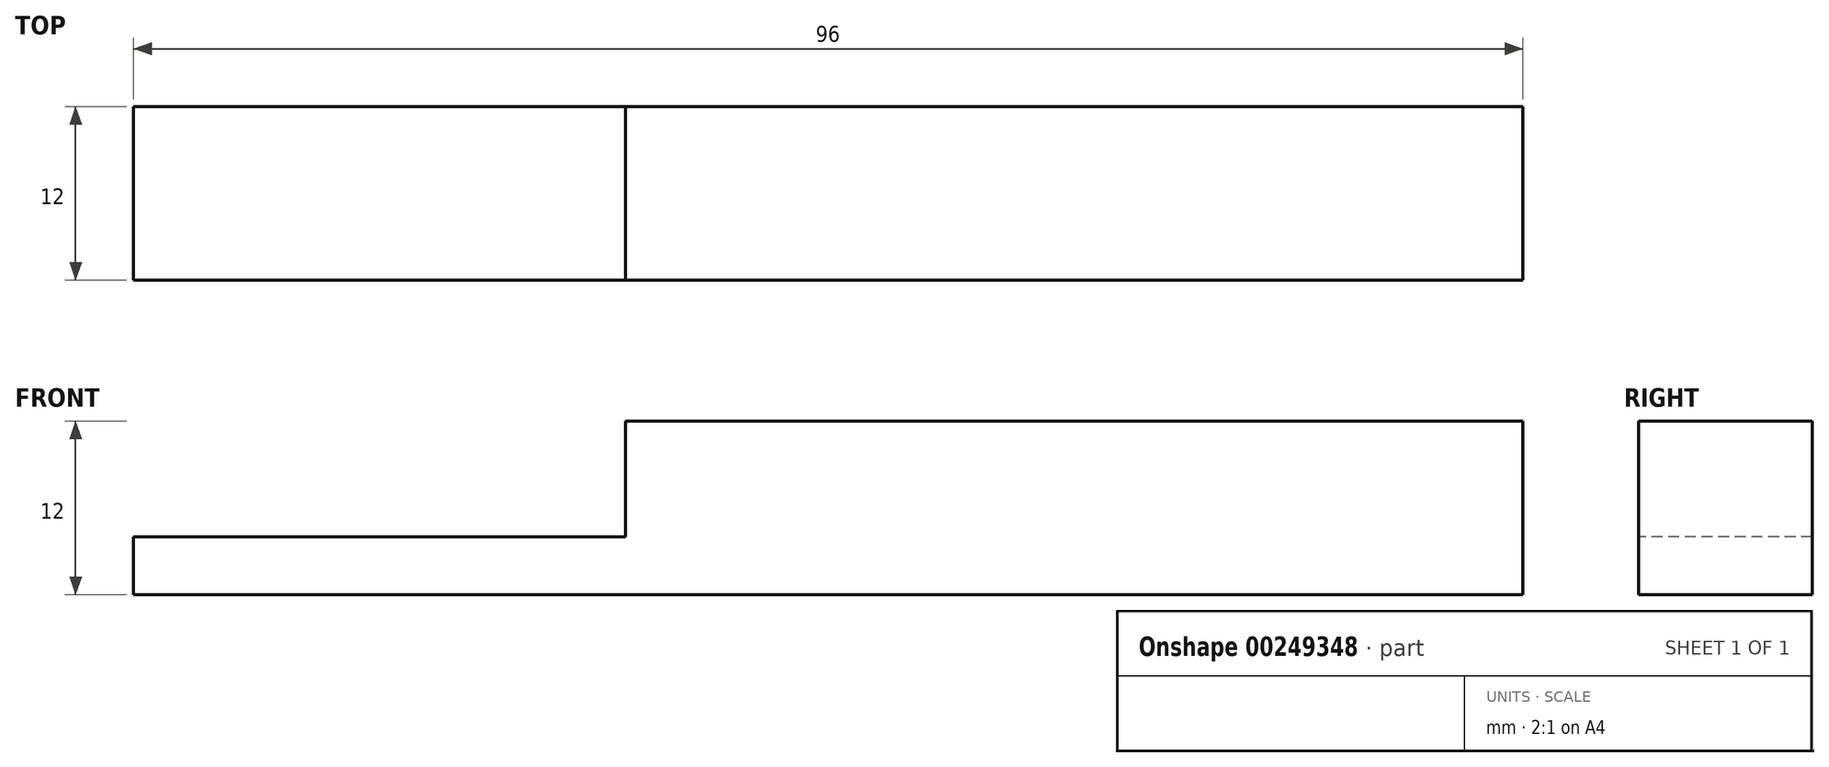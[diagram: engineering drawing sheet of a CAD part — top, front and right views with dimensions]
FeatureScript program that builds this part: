
annotation { "Feature Type Name" : "Feature", "Feature Type Description" : "" }
export const myFeature = defineFeature(function(context is Context, id is Id, definition is map)
    precondition{}
    {
        {
            var Q0;
            Q0=qCreatedBy(makeId("Front.planeOp"),FACE);
            var sketch = newSketch(context, id + "F0", { "sketchPlane" : qUnion([Q0])});
            skLineSegment(sketch, "E0.bottom", {"start": v(21, -96) * mm, "end": v(55, -96) * mm});
            skLineSegment(sketch, "E0.top", {"start": v(21, -100) * mm, "end": v(117, -100) * mm});
            skLineSegment(sketch, "E0.left", {"start": v(21, -96) * mm, "end": v(21, -100) * mm});
            skLineSegment(sketch, "E1", {"start": v(55, -96) * mm, "end": v(55, -88) * mm});
            skLineSegment(sketch, "E2", {"start": v(55, -88) * mm, "end": v(117, -88) * mm});
            skLineSegment(sketch, "E3", {"start": v(117, -88) * mm, "end": v(117, -100) * mm});
            skSolve(sketch);
        }
        {
            var Q0;
            Q0=makeQuery(id+"F0.imprint","IMPRINT",FACE,{"disambiguationData":[TD([[makeQuery(id+"F0.imprint","IMPRINT",EDGE,{"derivedFrom":sQuery(id+"F0.wireOp",EDGE,"cf6eb3bc-286c-4004-bd29-a7614bdbbe24.0")}),1.0]])]});
            var Q1;
            Q1=makeQuery(id+"F0.imprint","IMPRINT",FACE,{"disambiguationData":[TD([[makeQuery(id+"F0.imprint","IMPRINT",EDGE,{"derivedFrom":sQuery(id+"F0.wireOp",EDGE,"E0.bottom")}),-1.0]])]});
            extrude(context, id + "F1", {"entities" : qUnion([Q0, Q1]), "oppositeDirection" : true, "depth" : 12 * mm});
        }
    });
